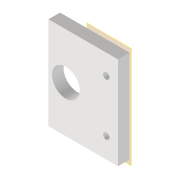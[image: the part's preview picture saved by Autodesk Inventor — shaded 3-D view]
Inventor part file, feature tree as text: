
AUTODESK INVENTOR PART (.ipt)
format: ipt  version: 2022 (Build 260153000, 153)  size: 95,232 bytes
history: native  units: mm
features: other x3, reference x2, plane x1, extrude x1, sketch x1
ambient origin geometry x8: Origin, YZ Plane, XZ Plane, XY Plane, X Axis, Y Axis, Z Axis, Center Point
bodies: Volumenkörper1 (feature_tree)
feature tree (8):
  plane  "Arbeitsebene1"
  extrude  "Extrusion1"  Depth=5.0mm
  sketch  "Skizze1"  dims[d0=30.0mm d1=12.0mm d2=50.0mm d3=5.0mm d4=0.0mm]
  reference  "Referenz1"
  reference  "Referenz2"
  other  "Assembly_XYZ_Stage_Micrometer_ontop.iam"
  other  "40_XYZstage_micrometer_motorized_nema8_lightsheet_samplemount_ontop:1"
  other  "40_XYZstage_micrometer_motorized_nema8_cube_ontop:1"
